# Revit family: EKF_EE_КаркасВРУ-1UnitS_IP54_PROxima
name_source: partatom
category: Электрооборудование
units: mm (PartAtom-declared; Revit-internal decimal feet)

## family parameters
Всегда вертикально = Нет
На основе рабочей плоскости = Да
Общий = Да
При загрузке вырезать с полостями = Нет
Размер круглого соединителя = Использовать диаметр
Тип детали = Силовой щит
Точка расчета площади = Нет

## types (4) — shared parameters
ADSK_Единица измерения = шт.
ADSK_Завод-изготовитель = EKF
ADSK_Количество = 1
ADSK_Марка = Каркас ВРУ-1 Unit S
ADSK_Материал = RAL 7035_Сталь
ADSK_Обозначение = Каркас ВРУ-1 Unit S
ADSK_Размер_Глубина = 450 мм
D = 9 мм
t = 1 мм
ВертПроф_Отступ = 30 мм
Изготовитель = EKF
Отступ = 20 мм
РейкаПопереч_Шаг = 759 мм
Серия номенклатуры = Unit PROxima
Степень защиты IP = IP54
Стойка_a = 24 мм
ТВ = EKF_2
Тип установки = Напольный
Ц450х450 = Вл_EKF_EE_ЦокольВРУUNIT_PROxima : Цоколь к ВРУ Unit S IP31 (Вх450х450) EKF PROxima
Ц600х450 = Вл_EKF_EE_ЦокольВРУUNIT_PROxima : Цоколь к ВРУ Unit S IP31 (Вх600х450) EKF PROxima
Ц600х600 = Вл_EKF_EE_ЦокольВРУUNIT_PROxima : Цоколь к ВРУ Unit S IP31 (Вх600х600) EKF PROxima
Ц800х450 = Вл_EKF_EE_ЦокольВРУUNIT_PROxima : Цоколь к ВРУ Unit S IP31 (Вх800х450) EKF PROxima
Ц800х600 = Вл_EKF_EE_ЦокольВРУUNIT_PROxima : Цоколь к ВРУ Unit S IP31 (Вх800х600) EKF PROxima
zero-valued in all types: ADSK_Масса, Отметка по умолчанию

## per-type parameters (varying)
| type | ADSK_Код изделия | ADSK_Размер_Высота | ADSK_Размер_Ширина | Стойка_h | Тип | Цоколь |
| Каркас ВРУ-1 Unit S сварной (1800х600х450) IP54 EKF PROxima | mb15-05-54m | 1800 мм | 600 мм | 1780 мм | 104 мм | Вл_EKF_EE_ЦокольВРУUNIT_PROxima : Цоколь к ВРУ Unit S IP31 (Вх600х450) EKF PROxima |
| Каркас ВРУ-1 Unit S сварной (1800х800х450) IP54 EKF PROxima | mb-18-80-45m | 1800 мм | 800 мм | 1780 мм | 105 мм | Вл_EKF_EE_ЦокольВРУUNIT_PROxima : Цоколь к ВРУ Unit S IP31 (Вх800х450) EKF PROxima |
| Каркас ВРУ-1 Unit S сварной (2000х600х450) IP54 EKF PROxima | mb15-20-60m | 2000 мм | 600 мм | 1980 мм | 106 мм | Вл_EKF_EE_ЦокольВРУUNIT_PROxima : Цоколь к ВРУ Unit S IP31 (Вх600х450) EKF PROxima |
| Каркас ВРУ-1 Unit S сварной (2000х800х450) IP54 EKF PROxima | mb15-09-54m | 2000 мм | 800 мм | 1980 мм | 107 мм | Вл_EKF_EE_ЦокольВРУUNIT_PROxima : Цоколь к ВРУ Unit S IP31 (Вх800х450) EKF PROxima |

note: column(s) folded — value = type name in every type: ADSK_Наименование
